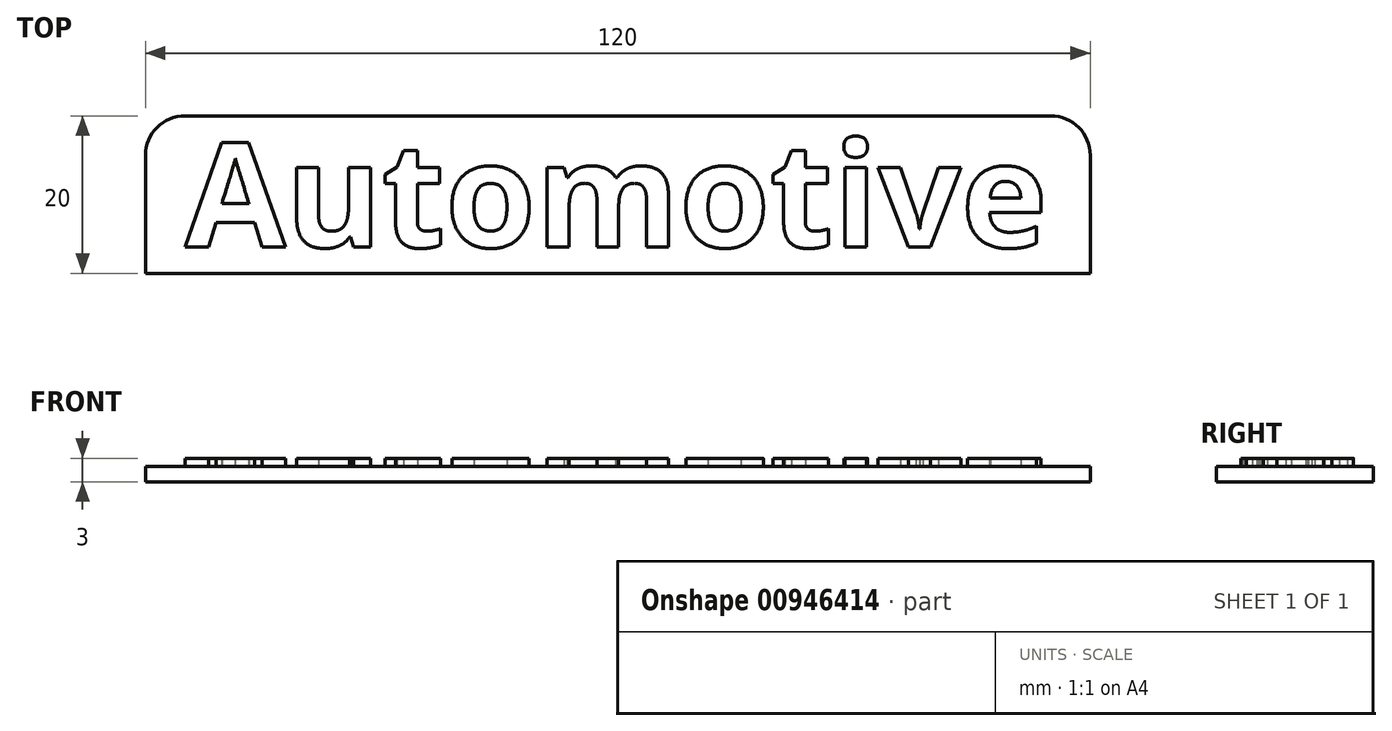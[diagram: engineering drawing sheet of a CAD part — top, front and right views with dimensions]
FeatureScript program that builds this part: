
annotation { "Feature Type Name" : "Feature", "Feature Type Description" : "" }
export const myFeature = defineFeature(function(context is Context, id is Id, definition is map)
    precondition{}
    {
        {
            var Q0;
            Q0=qCreatedBy(makeId("Top.planeOp"),FACE);
            var sketch = newSketch(context, id + "F0", { "sketchPlane" : qUnion([Q0])});
            skLineSegment(sketch, "E0.bottom", {"start": v(-60, 10) * mm, "end": v(60, 10) * mm});
            skLineSegment(sketch, "E0.top", {"start": v(-60, -10) * mm, "end": v(60, -10) * mm});
            skLineSegment(sketch, "E0.left", {"start": v(-60, 10) * mm, "end": v(-60, -10) * mm});
            skLineSegment(sketch, "E0.right", {"start": v(60, 10) * mm, "end": v(60, -10) * mm});
            skPoint(sketch, "E0.middle", {"position": v(0, 0) * mm});
            skSolve(sketch);
        }
        {
            var Q0;
            Q0 = qSketchRegion(id + "F0", true);
            extrude(context, id + "F1", {"entities" : qUnion([Q0]), "depth" : 2 * mm, "offsetDistance" : 25 * mm});
        }
        {
            var Q0;
            Q0=makeQuery(id+"F1.opExtrude","CAP_FACE",FACE,{"disambiguationData":[OSD([sQuery(id+"F0.wireOp",EDGE,"E0.bottom"),sQuery(id+"F0.wireOp",EDGE,"E0.top"),sQuery(id+"F0.wireOp",EDGE,"E0.left"),sQuery(id+"F0.wireOp",EDGE,"E0.right")])],"isStart":false});
            var sketch = newSketch(context, id + "F2", { "sketchPlane" : qUnion([Q0])});
            skText(sketch, "E1", { "text": "Automotive\n", "fontName": "OpenSans-Bold.ttf"});
            const initialGuessF2  = {"E1": [-0.055, -0.00667, 1, 0, 0.01337]};
            skSetInitialGuess(sketch, initialGuessF2);
            skSolve(sketch);
        }
        {
            var Q0;
            Q0 = qSketchRegion(id + "F2", true);
            extrude(context, id + "F3", {"entities" : qUnion([Q0]), "operationType" : NewBodyOperationType.ADD, "depth" : 1 * mm, "offsetDistance" : 25 * mm});
        }
        {
            var Q0;
            Q0=makeQuery(id+"F1.opExtrude","SWEPT_EDGE",EDGE,{"disambiguationData":[OSD([sQuery(id+"F0.wireOp",EDGE,"E0.bottom"),sQuery(id+"F0.wireOp",EDGE,"E0.left")])]});
            var Q1;
            Q1=makeQuery(id+"F1.opExtrude","SWEPT_EDGE",EDGE,{"disambiguationData":[OSD([sQuery(id+"F0.wireOp",EDGE,"E0.bottom"),sQuery(id+"F0.wireOp",EDGE,"E0.right")])]});
            fillet(context, id + "F4", {"entities" : qUnion([Q0, Q1]), "radius" : 5 * mm, "tangentPropagation" : true, "allowEdgeOverflow" : false});
        }
    });
